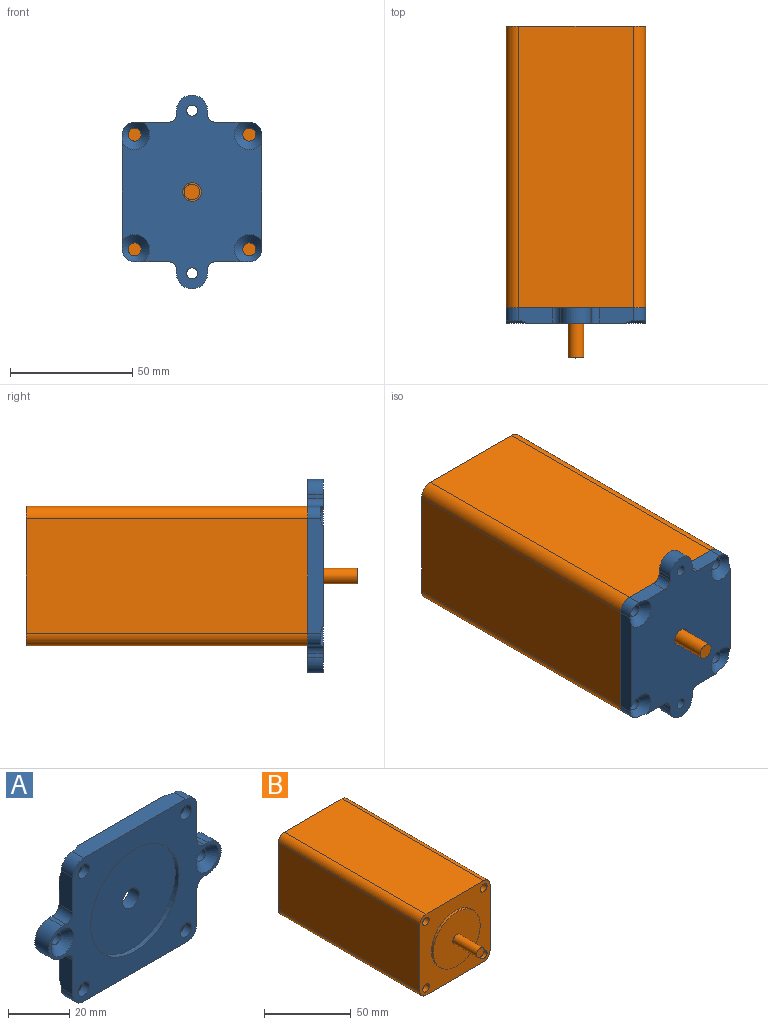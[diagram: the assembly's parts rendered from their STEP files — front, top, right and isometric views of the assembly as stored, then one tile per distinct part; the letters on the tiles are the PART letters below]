
ASSEMBLY  parts=2 mates=1
PART A: 37 faces, bbox 79.4x6.4x59.2 mm
  f0: cylinder r=3.81mm len=7.62mm, axis (0,1,0), area 109.4mm2, adj f28,f30
  f1: cylinder r=3.17mm len=6.35mm, axis (0,1,0), area 31.7mm2, adj f2,f25,f27,f28
  f2: plane 13.97x6.35mm, normal (-1,0,0), area 86.5mm2, adj f1,f3,f27,f28,f33
  f3: cylinder r=5.08mm len=5.33mm, axis (0,1,0), area 42.6mm2, adj f2,f4,f27,f33
  f4: plane 46.99x6.35mm, normal (0,0,-1), area 293.9mm2, adj f3,f5,f27,f28,f33,f34
  f5: cylinder r=5.08mm len=5.33mm, axis (0,1,0), area 42.6mm2, adj f4,f6,f27,f34
  f6: plane 13.97x6.35mm, normal (1,0,0), area 86.5mm2, adj f5,f7,f27,f28,f34
  f7: cylinder r=3.17mm len=6.35mm, axis (0,1,0), area 31.7mm2, adj f6,f8,f27,f28
  f8: plane 6.35x1.59mm, normal (0,0,-1), area 10.1mm2, adj f7,f9,f27,f28
  f9: cylinder r=6.35mm len=12.7mm, axis (0,1,0), area 126.7mm2, adj f8,f10,f27,f28
  f10: plane 6.35x1.59mm, normal (0,0,1), area 10.1mm2, adj f9,f11,f27,f28
  f11: cylinder r=3.17mm len=6.35mm, axis (0,1,0), area 31.7mm2, adj f10,f12,f27,f28
  f12: plane 13.97x6.35mm, normal (1,0,0), area 86.5mm2, adj f11,f13,f27,f28,f36
  f13: cylinder r=5.08mm len=5.33mm, axis (0,1,0), area 42.6mm2, adj f12,f14,f27,f36
  f14: plane 46.99x6.35mm, normal (0,0,1), area 293.9mm2, adj f13,f15,f27,f28,f35,f36
  f15: cylinder r=5.08mm len=5.33mm, axis (0,1,0), area 42.6mm2, adj f14,f16,f27,f35
  f16: plane 13.97x6.35mm, normal (-1,0,0), area 86.5mm2, adj f15,f17,f27,f28,f35
  f17: cylinder r=3.17mm len=6.35mm, axis (0,1,0), area 31.7mm2, adj f16,f18,f27,f28
  f18: plane 6.35x1.59mm, normal (0,0,1), area 10.1mm2, adj f17,f19,f27,f28
  f19: cylinder r=6.35mm len=12.7mm, axis (0,1,0), area 126.7mm2, adj f18,f25,f27,f28
  f20: cylinder r=2.67mm len=5.33mm, axis (0,1,0), area 48.9mm2, adj f27,f33
  f21: cylinder r=2.67mm len=5.33mm, axis (0,1,0), area 48.9mm2, adj f27,f35
  f22: cylinder r=2.67mm len=5.33mm, axis (0,1,0), area 48.9mm2, adj f27,f36
  f23: cylinder r=2.25mm len=4.5mm, axis (0,1,0), area 48.4mm2, adj f28,f32
  f24: cylinder r=2.25mm len=4.5mm, axis (0,1,0), area 48.4mm2, adj f28,f31
  f25: plane 6.35x1.59mm, normal (0,0,-1), area 10.1mm2, adj f1,f19,f27,f28
  f26: cylinder r=2.67mm len=5.33mm, axis (0,1,0), area 48.9mm2, adj f27,f34
  f27: plane 79.38x57.15mm, normal (0,-1,0), area 1945.8mm2, adj f1,f2,f3,f4,f5,f6,f7,f8
  f28: plane 79.38x57.15mm, normal (0,1,0), area 3010.2mm2, adj f0,f1,f2,f4,f6,f7,f8,f9
  f29: cylinder r=20.32mm len=40.64mm, axis (0,-1,0), area 227mm2, adj f27,f30
  f30: plane 40.64x40.64mm, normal (0,-1,0), area 1251.6mm2, adj f0,f29
  f31: cone r=2.25mm half-angle=45deg, axis (0,-1,0), area 96.3mm2, adj f24,f27
  f32: cone r=2.25mm half-angle=45deg, axis (0,-1,0), area 96.3mm2, adj f23,f27
  f33: cone r=6.1mm half-angle=45deg, axis (0,1,0), area 114.3mm2, adj f2,f3,f4,f20,f28
  f34: cone r=6.1mm half-angle=45deg, axis (0,1,0), area 114.3mm2, adj f4,f5,f6,f26,f28
  f35: cone r=6.1mm half-angle=45deg, axis (0,1,0), area 114.3mm2, adj f14,f15,f16,f21,f28
  f36: cone r=6.1mm half-angle=45deg, axis (0,1,0), area 114.3mm2, adj f12,f13,f14,f22,f28
PART B: 22 faces, bbox 57.2x135.9x57.2 mm
  f0: plane 57.15x57.15mm, normal (0,-1,0), area 2014.5mm2, adj f1,f2,f3,f4,f6,f7,f8,f9
  f1: plane 115.32x46.99mm, normal (-1,0,0), area 5418.7mm2, adj f0,f5,f6,f9
  f2: plane 115.32x46.99mm, normal (0,0,-1), area 5418.7mm2, adj f0,f5,f6,f7
  f3: plane 115.32x46.99mm, normal (1,0,0), area 5418.7mm2, adj f0,f5,f7,f8
  f4: plane 115.32x46.99mm, normal (0,0,1), area 5418.7mm2, adj f0,f5,f8,f9
  f5: plane 57.15x57.15mm, normal (0,1,0), area 3244mm2, adj f1,f2,f3,f4,f6,f7,f8,f9
  f6: cylinder r=5.08mm len=115.32mm, axis (0,-1,0), area 920.2mm2, adj f0,f1,f2,f5
  f7: cylinder r=5.08mm len=115.32mm, axis (0,1,0), area 920.2mm2, adj f0,f2,f3,f5
  f8: cylinder r=5.08mm len=115.32mm, axis (0,-1,0), area 920.2mm2, adj f0,f3,f4,f5
  f9: cylinder r=5.08mm len=115.32mm, axis (0,1,0), area 920.2mm2, adj f0,f1,f4,f5
  f10: cylinder r=19.05mm len=38.1mm, axis (0,1,0), area 182.4mm2, adj f0,f11
  f11: plane 38.1x38.1mm, normal (0,-1,0), area 1108.4mm2, adj f10,f12
  f12: cylinder r=3.17mm len=19.05mm, axis (0,1,0), area 380mm2, adj f11,f13
  f13: plane 6.35x6.35mm, normal (0,-1,0), area 31.7mm2, adj f12
  f14: cylinder r=2.67mm len=25.4mm, axis (0,-1,0), area 425.6mm2, adj f0,f15
  f15: plane 5.33x5.33mm, normal (0,-1,0), area 22.3mm2, adj f14
  f16: cylinder r=2.67mm len=25.4mm, axis (0,-1,0), area 425.6mm2, adj f0,f17
  f17: plane 5.33x5.33mm, normal (0,-1,0), area 22.3mm2, adj f16
  f18: cylinder r=2.67mm len=25.4mm, axis (0,-1,0), area 425.6mm2, adj f0,f19
  f19: plane 5.33x5.33mm, normal (0,-1,0), area 22.3mm2, adj f18
  f20: cylinder r=2.67mm len=25.4mm, axis (0,-1,0), area 425.6mm2, adj f0,f21
  f21: plane 5.33x5.33mm, normal (0,-1,0), area 22.3mm2, adj f20
PLACE A rot(axis=(0.71,0,-0.71),180deg) t=(31.89,-110.47,26.2)mm
PLACE B t=(3.32,11.19,-2.38)mm
MATE fastened A.f15 <-> B.f9  axis (0,1,0) through (8.4,-104.12,49.69)mm
